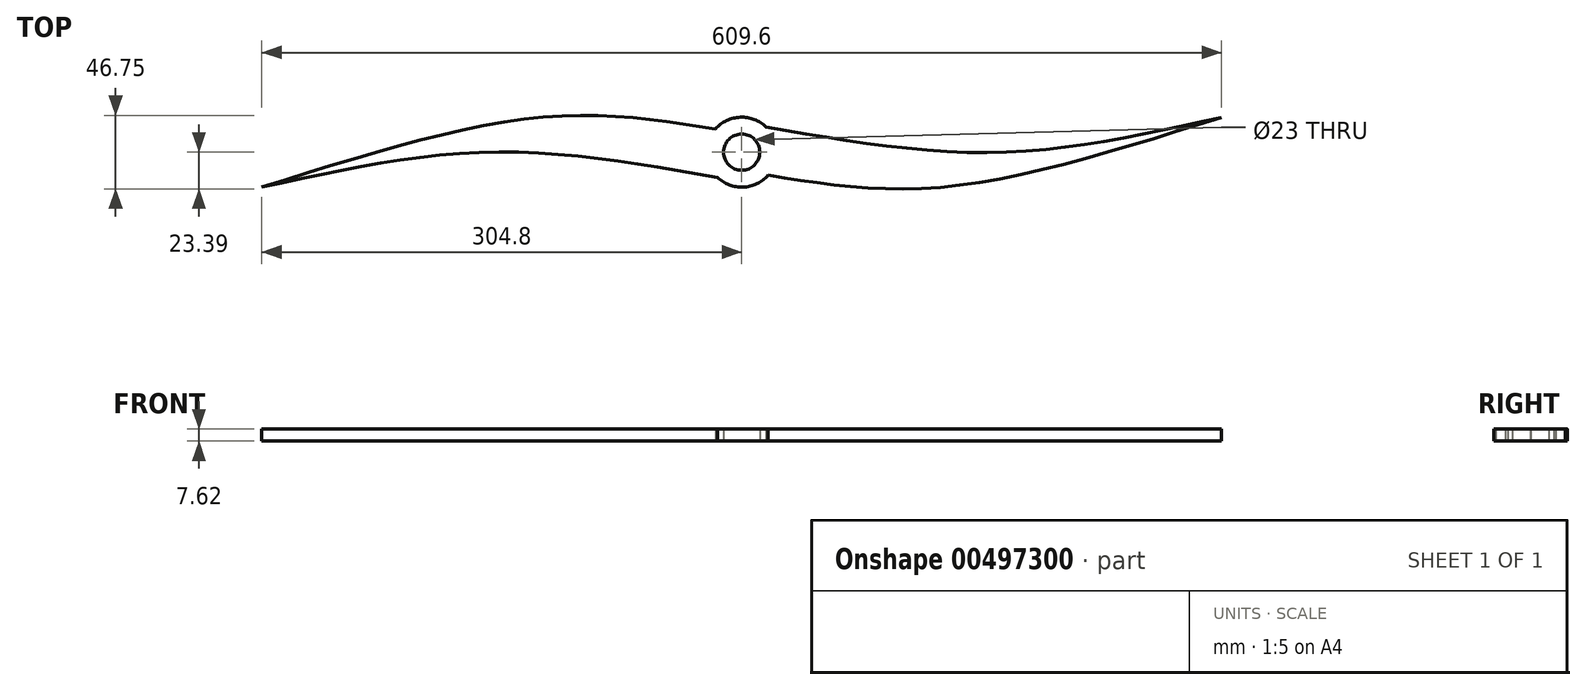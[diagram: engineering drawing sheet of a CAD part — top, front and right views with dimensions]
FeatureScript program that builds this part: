
annotation { "Feature Type Name" : "Feature", "Feature Type Description" : "" }
export const myFeature = defineFeature(function(context is Context, id is Id, definition is map)
    precondition{}
    {
        {
            var Q0;
            Q0=qCreatedBy(makeId("Top.planeOp"),FACE);
            var sketch = newSketch(context, id + "F0", { "sketchPlane" : qUnion([Q0])});
            skArc(sketch, "E0", {"start": v(-15.45, -15.97) * mm, "mid": v(0.9, -22.2) * mm, "end": v(16.7, -14.66) * mm});
            skArc(sketch, "E1.trimOffspring", {"start": v(15.45, 15.97) * mm, "mid": v(-0.9, 22.2) * mm, "end": v(-16.7, 14.66) * mm});
            skCircle(sketch, "E2", {"center": v(0, 0) * mm, "radius": 11.5 * mm});
            skLineSegment(sketch, "E3", {"start": v(-304.8, 22.23) * mm, "end": v(334.36, 22.23) * mm, "construction": true});
            skLineSegment(sketch, "E4", {"start": v(0, 0) * mm, "end": v(228.42, 0) * mm, "construction": true});
            skLineSegment(sketch, "E5.MirrorCS", {"start": v(-304.8, -22.23) * mm, "end": v(334.36, -22.23) * mm, "construction": true});
            skLineSegment(sketch, "E6", {"start": v(-304.8, 22.23) * mm, "end": v(-304.8, -22.23) * mm, "construction": true});
            skLineSegment(sketch, "E7", {"start": v(334.36, 22.23) * mm, "end": v(334.36, -22.23) * mm, "construction": true});
            skFitSpline(sketch, "E8", {"points": [v(-304.8, -22.23) * mm, v(-160.51, 0) * mm, v(-15.45, -15.97) * mm], "startDerivative": vector(291.08, 63.47) * mm, "endDerivative": vector(290.93, -51.07) * mm});
            skFitSpline(sketch, "E9", {"points": [v(-304.8, -22.23) * mm, v(-126.47, 22.23) * mm, v(-16.7, 14.66) * mm], "startDerivative": vector(337.4, 105.83) * mm, "endDerivative": vector(237.8, -38.3) * mm});
            skFitSpline(sketch, "E10.MirrorCS", {"points": [v(304.8, 22.1) * mm, v(126.53, -22.27) * mm, v(16.7, -14.66) * mm], "startDerivative": vector(-337.4, -105.83) * mm, "endDerivative": vector(-237.8, 38.3) * mm});
            skFitSpline(sketch, "E11.MirrorCS", {"points": [v(304.8, 22.1) * mm, v(163.19, -0.13) * mm, v(15.45, 15.97) * mm], "startDerivative": vector(-291.08, -63.47) * mm, "endDerivative": vector(-290.93, 51.07) * mm});
            skSolve(sketch);
        }
        {
            var Q0;
            Q0 = qSketchRegion(id + "F0", true);
            extrude(context, id + "F1", {"entities" : qUnion([Q0]), "depth" : 7.62 * mm, "offsetDistance" : 25.4 * mm});
        }
    });
